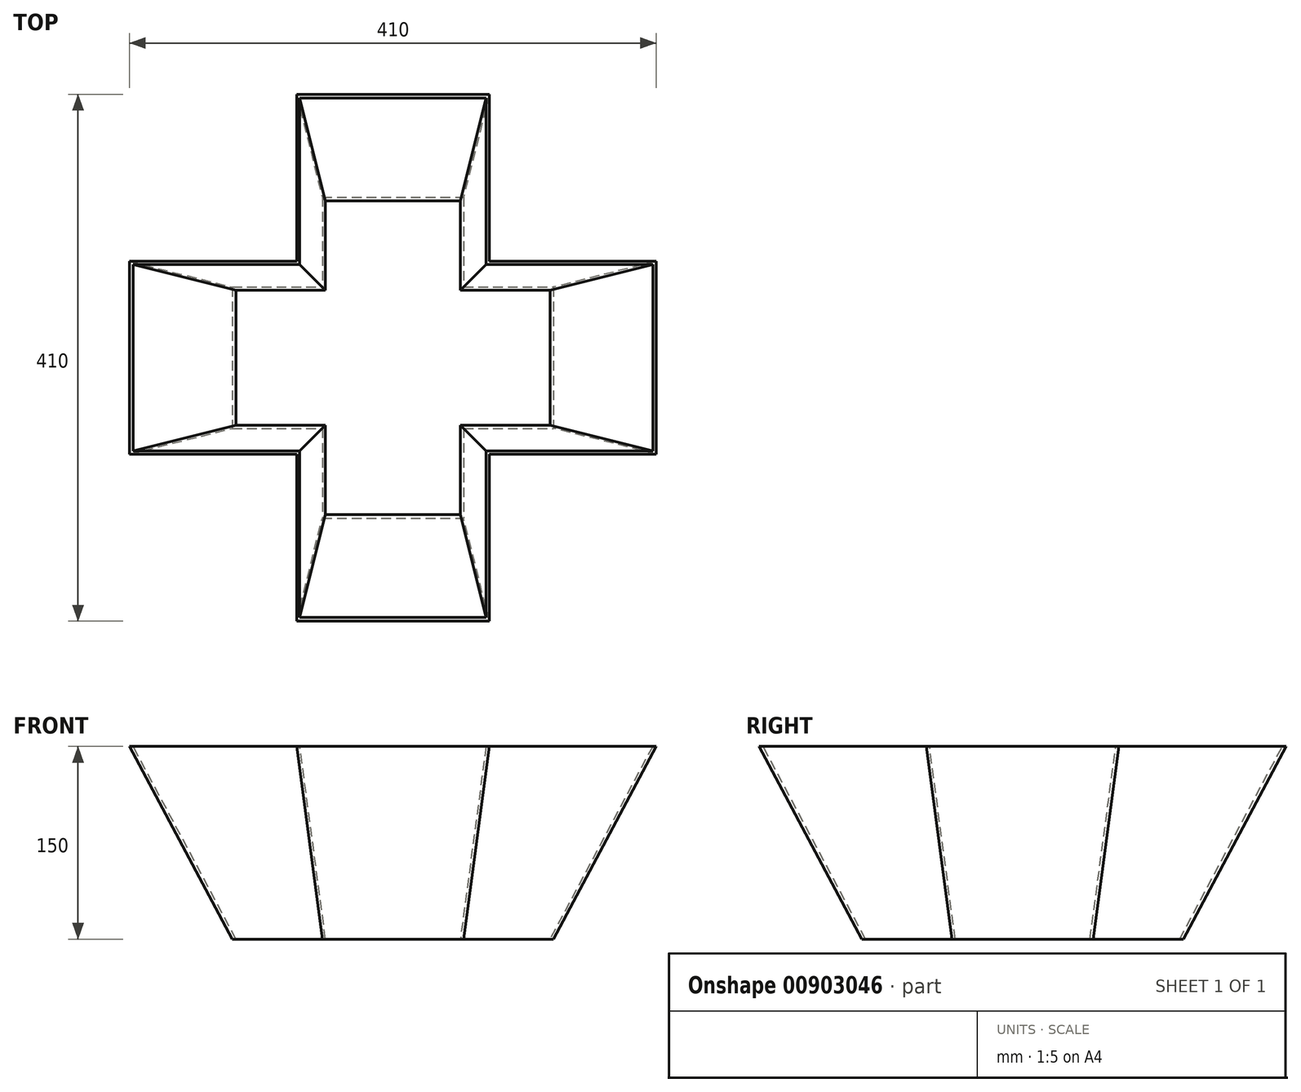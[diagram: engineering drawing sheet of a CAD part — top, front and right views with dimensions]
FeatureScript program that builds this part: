
annotation { "Feature Type Name" : "Feature", "Feature Type Description" : "" }
export const myFeature = defineFeature(function(context is Context, id is Id, definition is map)
    precondition{}
    {
        {
            var Q0;
            Q0=qCreatedBy(makeId("Top.planeOp"),FACE);
            var sketch = newSketch(context, id + "F0", { "sketchPlane" : qUnion([Q0])});
            skLineSegment(sketch, "E0.bottom", {"start": v(-55, 125) * mm, "end": v(55, 125) * mm});
            skLineSegment(sketch, "E0.top", {"start": v(-55, -125) * mm, "end": v(55, -125) * mm});
            skLineSegment(sketch, "E0.left", {"start": v(-55, 125) * mm, "end": v(-55, 55) * mm});
            skLineSegment(sketch, "E0.right", {"start": v(55, 125) * mm, "end": v(55, 55) * mm});
            skLineSegment(sketch, "E1.bottom", {"start": v(-125, 55) * mm, "end": v(-55, 55) * mm});
            skLineSegment(sketch, "E1.top", {"start": v(-125, -55) * mm, "end": v(-55, -55) * mm});
            skLineSegment(sketch, "E1.left", {"start": v(-125, 55) * mm, "end": v(-125, -55) * mm});
            skLineSegment(sketch, "E1.right", {"start": v(125, 55) * mm, "end": v(125, -55) * mm});
            skLineSegment(sketch, "E2.trimOffspring", {"start": v(55, 55) * mm, "end": v(125, 55) * mm});
            skLineSegment(sketch, "E3.trimOffspring", {"start": v(-55, -55) * mm, "end": v(-55, -125) * mm});
            skLineSegment(sketch, "E4.trimOffspring", {"start": v(55, -55) * mm, "end": v(55, -125) * mm});
            skLineSegment(sketch, "E5.trimOffspring", {"start": v(55, -55) * mm, "end": v(125, -55) * mm});
            skSolve(sketch);
        }
        {
            var Q0;
            Q0=qCreatedBy(makeId("Top.planeOp"),FACE);
            cPlane(context, id + "F1", {"entities" : qUnion([Q0]), "cplaneType" : CPlaneType.OFFSET, "offset" : 150 * mm, "width" : 150 * mm, "height" : 150 * mm});
        }
        {
            var Q0;
            Q0=qCreatedBy(id+"F1.planeOp",FACE);
            var sketch = newSketch(context, id + "F2", { "sketchPlane" : qUnion([Q0])});
            skLineSegment(sketch, "E6.bottom", {"start": v(-205, -75) * mm, "end": v(-75, -75) * mm});
            skLineSegment(sketch, "E6.top", {"start": v(-205, 75) * mm, "end": v(-75, 75) * mm});
            skLineSegment(sketch, "E6.left", {"start": v(-205, -75) * mm, "end": v(-205, 75) * mm});
            skLineSegment(sketch, "E6.right", {"start": v(205, -75) * mm, "end": v(205, 75) * mm});
            skLineSegment(sketch, "E7.bottom", {"start": v(-75, -205) * mm, "end": v(75, -205) * mm});
            skLineSegment(sketch, "E7.top", {"start": v(-75, 205) * mm, "end": v(75, 205) * mm});
            skLineSegment(sketch, "E7.left", {"start": v(-75, -205) * mm, "end": v(-75, -75) * mm});
            skLineSegment(sketch, "E7.right", {"start": v(75, -205) * mm, "end": v(75, -75) * mm});
            skLineSegment(sketch, "E8.trimOffspring", {"start": v(-75, 75) * mm, "end": v(-75, 205) * mm});
            skLineSegment(sketch, "E9.trimOffspring", {"start": v(75, -75) * mm, "end": v(205, -75) * mm});
            skLineSegment(sketch, "E10.trimOffspring", {"start": v(75, 75) * mm, "end": v(75, 205) * mm});
            skLineSegment(sketch, "E11.trimOffspring", {"start": v(75, 75) * mm, "end": v(205, 75) * mm});
            skSolve(sketch);
        }
        {
            var Q0;
            Q0=makeQuery(id+"F2.imprint","IMPRINT",FACE,{"disambiguationData":[TD([[makeQuery(id+"F2.imprint","IMPRINT",EDGE,{"derivedFrom":sQuery(id+"F2.wireOp",EDGE,"E6.bottom")}),1.0]])]});
            var Q1;
            Q1=makeQuery(id+"F0.imprint","IMPRINT",FACE,{"disambiguationData":[TD([[makeQuery(id+"F0.imprint","IMPRINT",EDGE,{"derivedFrom":sQuery(id+"F0.wireOp",EDGE,"E0.bottom")}),-1.0]])]});
            loft(context, id + "F3", {"sheetProfilesArray" : [{ "sheetProfileEntities" : qUnion([Q0]) }, { "sheetProfileEntities" : qUnion([Q1]) }]});
        }
        {
            var Q0;
            Q0=makeQuery(id+"F3.opLoft","CAP_FACE",FACE,{"disambiguationData":[OSD([makeQuery(id+"F2.imprint","IMPRINT",FACE,{"disambiguationData":[TD([[makeQuery(id+"F2.imprint","IMPRINT",EDGE,{"derivedFrom":sQuery(id+"F2.wireOp",EDGE,"E6.bottom")}),1.0]])]})])],"isStart":true});
            var Q1;
            Q1=makeQuery(id+"F3.opLoft","CAP_FACE",FACE,{"disambiguationData":[OSD([makeQuery(id+"F0.imprint","IMPRINT",FACE,{"disambiguationData":[TD([[makeQuery(id+"F0.imprint","IMPRINT",EDGE,{"derivedFrom":sQuery(id+"F0.wireOp",EDGE,"E0.bottom")}),-1.0]])]})])],"isStart":true});
            shell(context, id + "F4", {"entities" : qUnion([Q0, Q1]), "thickness" : 2.5 * mm});
        }
    });
